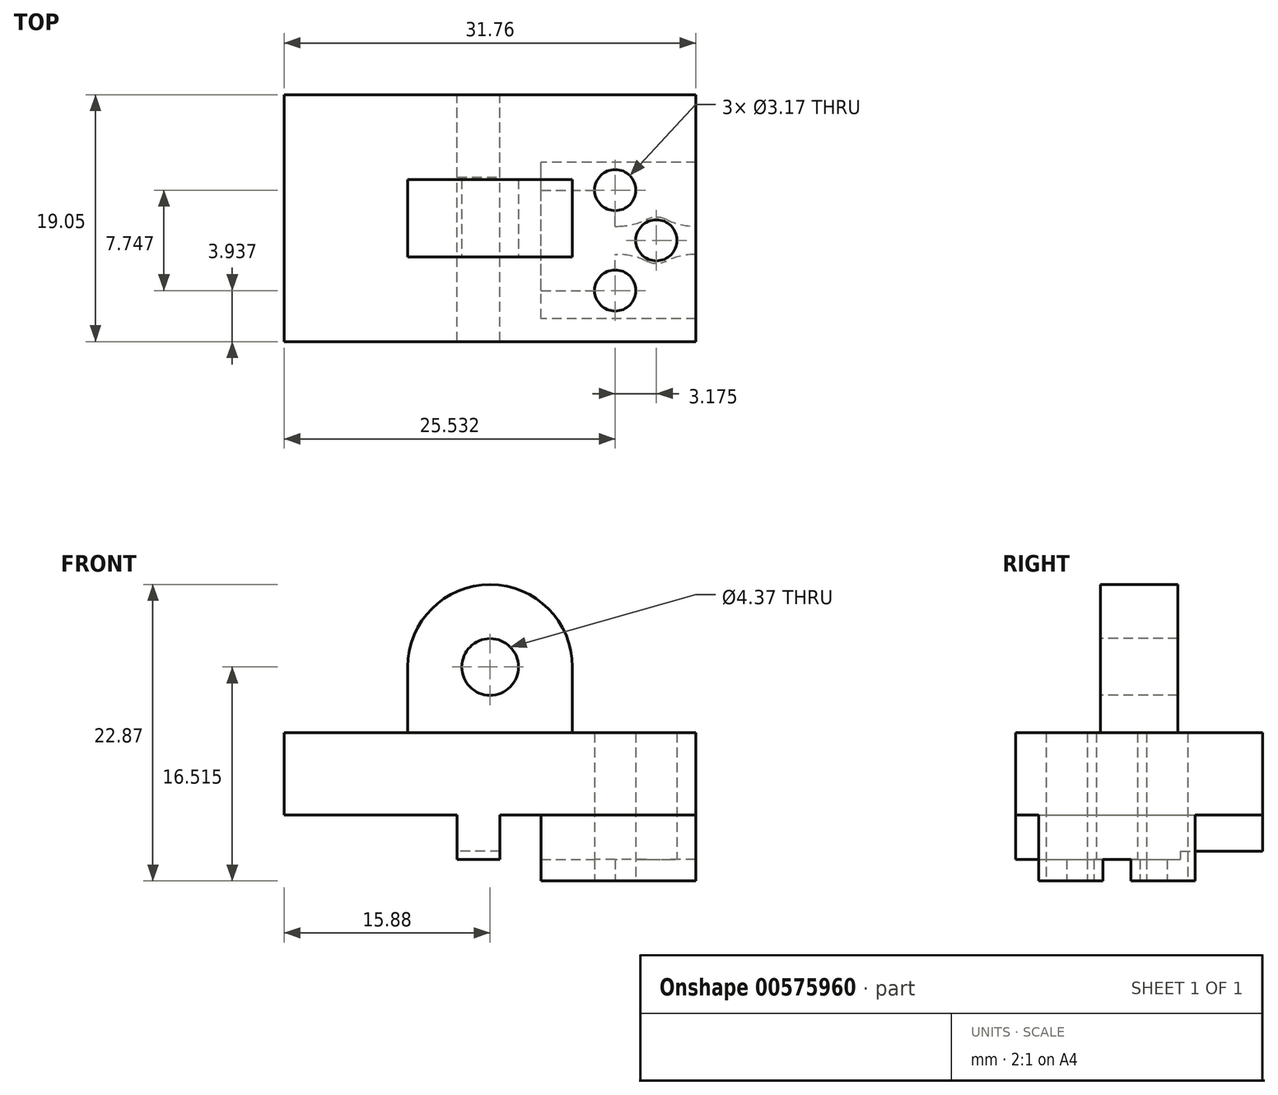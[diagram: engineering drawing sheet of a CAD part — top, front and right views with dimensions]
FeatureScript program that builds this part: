
annotation { "Feature Type Name" : "Feature", "Feature Type Description" : "" }
export const myFeature = defineFeature(function(context is Context, id is Id, definition is map)
    precondition{}
    {
        {
            var Q0;
            Q0=qCreatedBy(makeId("Front.planeOp"),FACE);
            var sketch = newSketch(context, id + "F0", { "sketchPlane" : qUnion([Q0])});
            skLineSegment(sketch, "E0.bottom", {"start": v(15.88, -3.18) * mm, "end": v(-15.88, -3.18) * mm});
            skLineSegment(sketch, "E0.top", {"start": v(15.88, 3.18) * mm, "end": v(-15.88, 3.18) * mm});
            skLineSegment(sketch, "E0.left", {"start": v(15.88, -3.18) * mm, "end": v(15.88, 3.18) * mm});
            skLineSegment(sketch, "E0.right", {"start": v(-15.88, -3.18) * mm, "end": v(-15.88, 3.17) * mm});
            skPoint(sketch, "E0.middle", {"position": v(0, 0) * mm});
            skSolve(sketch);
        }
        {
            var Q0;
            Q0=makeQuery(id+"F0.imprint","IMPRINT",FACE,{"disambiguationData":[TD([[makeQuery(id+"F0.imprint","IMPRINT",EDGE,{"derivedFrom":sQuery(id+"F0.wireOp",EDGE,"E0.bottom")}),-1.0]])]});
            extrude(context, id + "F1", {"entities" : qUnion([Q0]), "depth" : 19.05 * mm, "offsetDistance" : 25.4 * mm});
        }
        {
            var Q0;
            Q0=makeQuery(id+"F1.opExtrude","SWEPT_FACE",FACE,{"disambiguationData":[OSD([sQuery(id+"F0.wireOp",EDGE,"E0.top")])]});
            var sketch = newSketch(context, id + "F2", { "sketchPlane" : qUnion([Q0])});
            skLineSegment(sketch, "E1.bottom", {"start": v(6.35, -12.5) * mm, "end": v(-6.35, -12.5) * mm});
            skLineSegment(sketch, "E1.top", {"start": v(6.35, -6.54) * mm, "end": v(-6.35, -6.54) * mm});
            skLineSegment(sketch, "E1.left", {"start": v(6.35, -12.5) * mm, "end": v(6.35, -6.54) * mm});
            skLineSegment(sketch, "E1.right", {"start": v(-6.35, -12.5) * mm, "end": v(-6.35, -6.54) * mm});
            skPoint(sketch, "E1.middle", {"position": v(0, -9.53) * mm});
            skPoint(sketch, "E1.middle.positionSnap0", {"position": v(-15.88, -9.53) * mm});
            skPoint(sketch, "E1.centerSnap0", {"position": v(-15.88, -9.53) * mm});
            skSolve(sketch);
        }
        {
            var Q0;
            Q0=qSketchRegion(id+"F2",true);
            extrude(context, id + "F3", {"entities" : qUnion([Q0]), "operationType" : NewBodyOperationType.ADD, "depth" : 11.43 * mm, "offsetDistance" : 25.4 * mm});
        }
        {
            var Q0;
            Q0=makeQuery(id+"F3.opExtrude","CAP_EDGE",EDGE,{"disambiguationData":[OSD([sQuery(id+"F2.wireOp",EDGE,"E1.right")])],"isStart":false});
            var Q1;
            Q1=makeQuery(id+"F3.opExtrude","CAP_EDGE",EDGE,{"disambiguationData":[OSD([sQuery(id+"F2.wireOp",EDGE,"E1.left")])],"isStart":false});
            fillet(context, id + "F4", {"entities" : qUnion([Q0, Q1]), "radius" : 6.35 * mm, "tangentPropagation" : true, "allowEdgeOverflow" : false});
        }
        {
            var Q0;
            Q0=makeQuery(id+"F3.opExtrude","SWEPT_FACE",FACE,{"disambiguationData":[OSD([sQuery(id+"F2.wireOp",EDGE,"E1.bottom")])]});
            var sketch = newSketch(context, id + "F5", { "sketchPlane" : qUnion([Q0])});
            skCircle(sketch, "E2", {"center": v(0, 8.26) * mm, "radius": 2.18 * mm});
            skSolve(sketch);
        }
        {
            var Q0;
            Q0=qSketchRegion(id+"F5",true);
            extrude(context, id + "F6", {"entities" : qUnion([Q0]), "operationType" : NewBodyOperationType.REMOVE, "oppositeDirection" : true, "depth" : 25.4 * mm, "offsetDistance" : 25.4 * mm});
        }
        {
            var Q0;
            Q0=makeQuery(id+"F1.opExtrude","SWEPT_FACE",FACE,{"disambiguationData":[OSD([sQuery(id+"F0.wireOp",EDGE,"E0.bottom")])]});
            var sketch = newSketch(context, id + "F7", { "sketchPlane" : qUnion([Q0])});
            skLineSegment(sketch, "E3.bottom", {"start": v(15.88, 17.27) * mm, "end": v(3.94, 17.27) * mm});
            skLineSegment(sketch, "E3.top", {"start": v(15.88, 5.2) * mm, "end": v(3.94, 5.2) * mm});
            skLineSegment(sketch, "E3.left", {"start": v(15.88, 17.27) * mm, "end": v(15.88, 5.2) * mm});
            skLineSegment(sketch, "E3.right", {"start": v(3.94, 17.27) * mm, "end": v(3.94, 5.2) * mm});
            skSolve(sketch);
        }
        {
            var Q0;
            Q0=makeQuery(id+"F7.imprint","IMPRINT",FACE,{"disambiguationData":[TD([[makeQuery(id+"F7.imprint","IMPRINT",EDGE,{"derivedFrom":sQuery(id+"F7.wireOp",EDGE,"E3.bottom")}),1.0]])]});
            extrude(context, id + "F8", {"entities" : qUnion([Q0]), "operationType" : NewBodyOperationType.ADD, "depth" : 5.08 * mm, "offsetDistance" : 25.4 * mm});
        }
        {
            var Q0;
            Q0=makeQuery(id+"F8.opExtrude","CAP_FACE",FACE,{"disambiguationData":[OSD([sQuery(id+"F7.wireOp",EDGE,"E3.bottom"),sQuery(id+"F7.wireOp",EDGE,"E3.top"),sQuery(id+"F7.wireOp",EDGE,"E3.left"),sQuery(id+"F7.wireOp",EDGE,"E3.right")])],"isStart":false});
            var sketch = newSketch(context, id + "F9", { "sketchPlane" : qUnion([Q0])});
            skLineSegment(sketch, "E4.bottom", {"start": v(3.94, 15.11) * mm, "end": v(9.65, 15.11) * mm});
            skLineSegment(sketch, "E4.top", {"start": v(3.94, 7.37) * mm, "end": v(9.65, 7.37) * mm});
            skLineSegment(sketch, "E4.left", {"start": v(3.94, 15.11) * mm, "end": v(3.94, 7.37) * mm});
            skLineSegment(sketch, "E4.right", {"start": v(9.65, 15.11) * mm, "end": v(9.65, 7.37) * mm});
            skSolve(sketch);
        }
        {
            var Q0;
            Q0=makeQuery(id+"F9.imprint","IMPRINT",FACE,{"disambiguationData":[TD([[makeQuery(id+"F9.imprint","IMPRINT",EDGE,{"derivedFrom":sQuery(id+"F9.wireOp",EDGE,"E4.bottom")}),-1.0]])]});
            extrude(context, id + "F10", {"entities" : qUnion([Q0]), "operationType" : NewBodyOperationType.REMOVE, "oppositeDirection" : true, "depth" : 1.65 * mm, "offsetDistance" : 25.4 * mm});
        }
        {
            var Q0;
            Q0=makeQuery(id+"F8.opExtrude","CAP_FACE",FACE,{"disambiguationData":[OSD([sQuery(id+"F7.wireOp",EDGE,"E3.bottom"),sQuery(id+"F7.wireOp",EDGE,"E3.top"),sQuery(id+"F7.wireOp",EDGE,"E3.left"),sQuery(id+"F7.wireOp",EDGE,"E3.right")])],"isStart":false});
            var sketch = newSketch(context, id + "F11", { "sketchPlane" : qUnion([Q0])});
            skCircle(sketch, "E5", {"center": v(9.65, 15.11) * mm, "radius": 1.59 * mm});
            skCircle(sketch, "E6", {"center": v(9.65, 7.37) * mm, "radius": 1.59 * mm});
            skCircle(sketch, "E7", {"center": v(12.83, 11.24) * mm, "radius": 1.59 * mm});
            skPoint(sketch, "E7.centerSnap0", {"position": v(9.65, 11.24) * mm});
            skSolve(sketch);
        }
        {
            var Q0;
            Q0 = qSketchRegion(id + "F11", true);
            extrude(context, id + "F12", {"entities" : qUnion([Q0]), "operationType" : NewBodyOperationType.REMOVE, "oppositeDirection" : true, "depth" : 25.4 * mm, "offsetDistance" : 25.4 * mm});
        }
        {
            var Q0;
            Q0=makeQuery(id+"F1.opExtrude","SWEPT_FACE",FACE,{"disambiguationData":[OSD([sQuery(id+"F0.wireOp",EDGE,"E0.bottom")])]});
            var sketch = newSketch(context, id + "F13", { "sketchPlane" : qUnion([Q0])});
            skLineSegment(sketch, "E8.bottom", {"start": v(-2.54, 19.05) * mm, "end": v(0.76, 19.05) * mm});
            skLineSegment(sketch, "E8.top", {"start": v(-2.54, 0) * mm, "end": v(0.76, 0) * mm});
            skLineSegment(sketch, "E8.left", {"start": v(-2.54, 19.05) * mm, "end": v(-2.54, 0) * mm});
            skLineSegment(sketch, "E8.right", {"start": v(0.76, 19.05) * mm, "end": v(0.76, 0) * mm});
            skSolve(sketch);
        }
        {
            var Q0;
            Q0 = qSketchRegion(id + "F13", true);
            extrude(context, id + "F14", {"entities" : qUnion([Q0]), "operationType" : NewBodyOperationType.ADD, "depth" : 3.43 * mm, "offsetDistance" : 25.4 * mm});
        }
        {
            var Q0;
            Q0=makeQuery(id+"F14.opExtrude","CAP_FACE",FACE,{"disambiguationData":[OSD([sQuery(id+"F13.wireOp",EDGE,"E8.bottom"),sQuery(id+"F13.wireOp",EDGE,"E8.top"),sQuery(id+"F13.wireOp",EDGE,"E8.left"),sQuery(id+"F13.wireOp",EDGE,"E8.right")])],"isStart":false});
            var sketch = newSketch(context, id + "F15", { "sketchPlane" : qUnion([Q0])});
            skLineSegment(sketch, "E9.bottom", {"start": v(-2.54, 0) * mm, "end": v(0.76, 0) * mm});
            skLineSegment(sketch, "E9.top", {"start": v(-2.54, 6.35) * mm, "end": v(0.76, 6.35) * mm});
            skLineSegment(sketch, "E9.left", {"start": v(-2.54, 0) * mm, "end": v(-2.54, 6.35) * mm});
            skLineSegment(sketch, "E9.right", {"start": v(0.76, 0) * mm, "end": v(0.76, 6.35) * mm});
            skSolve(sketch);
        }
        {
            var Q0;
            Q0=makeQuery(id+"F15.imprint","IMPRINT",FACE,{"disambiguationData":[TD([[makeQuery(id+"F15.imprint","IMPRINT",EDGE,{"derivedFrom":sQuery(id+"F15.wireOp",EDGE,"E9.bottom")}),-1.0]])]});
            extrude(context, id + "F16", {"entities" : qUnion([Q0]), "operationType" : NewBodyOperationType.REMOVE, "oppositeDirection" : true, "depth" : 0.64 * mm, "offsetDistance" : 25.4 * mm});
        }
        {
            var Q0;
            Q0=makeQuery(id+"F8.opExtrude","CAP_FACE",FACE,{"disambiguationData":[OSD([sQuery(id+"F7.wireOp",EDGE,"E3.bottom"),sQuery(id+"F7.wireOp",EDGE,"E3.top"),sQuery(id+"F7.wireOp",EDGE,"E3.left"),sQuery(id+"F7.wireOp",EDGE,"E3.right")])],"isStart":false});
            var sketch = newSketch(context, id + "F17", { "sketchPlane" : qUnion([Q0])});
            skLineSegment(sketch, "E10.bottom", {"start": v(9.65, 12.32) * mm, "end": v(11.41, 12.32) * mm});
            skLineSegment(sketch, "E10.top", {"start": v(9.65, 10.16) * mm, "end": v(11.41, 10.16) * mm});
            skLineSegment(sketch, "E10.left", {"start": v(9.65, 12.32) * mm, "end": v(9.65, 10.16) * mm});
            skLineSegment(sketch, "E10.right", {"start": v(15.88, 12.32) * mm, "end": v(15.88, 10.16) * mm});
            skArc(sketch, "E11", {"start": v(11.41, 10.16) * mm, "mid": v(12.83, 9.46) * mm, "end": v(14.24, 10.16) * mm});
            skLineSegment(sketch, "E12.trimOffspring", {"start": v(14.24, 12.32) * mm, "end": v(15.88, 12.32) * mm});
            skLineSegment(sketch, "E13.trimOffspring", {"start": v(14.24, 10.16) * mm, "end": v(15.88, 10.16) * mm});
            skArc(sketch, "E14.trimOffspring", {"start": v(14.24, 12.32) * mm, "mid": v(12.83, 13.02) * mm, "end": v(11.41, 12.32) * mm});
            skSolve(sketch);
        }
        {
            var Q0;
            Q0 = qSketchRegion(id + "F17", true);
            extrude(context, id + "F18", {"entities" : qUnion([Q0]), "operationType" : NewBodyOperationType.REMOVE, "oppositeDirection" : true, "depth" : 1.65 * mm, "offsetDistance" : 25.4 * mm});
        }
        {
            var Q0;
            Q0=makeQuery(id+"F18.boolean.opBoolean","COPY",EDGE,{"derivedFrom":makeQuery(id+"F18.opExtrude","SWEPT_EDGE",EDGE,{"disambiguationData":[OSD([sQuery(id+"F17.wireOp",EDGE,"E10.bottom"),sQuery(id+"F17.wireOp",EDGE,"E14.trimOffspring")])]})});
            var Q1;
            Q1=makeQuery(id+"F18.boolean.opBoolean","COPY",EDGE,{"derivedFrom":makeQuery(id+"F18.opExtrude","SWEPT_EDGE",EDGE,{"disambiguationData":[OSD([sQuery(id+"F17.wireOp",EDGE,"E12.trimOffspring"),sQuery(id+"F17.wireOp",EDGE,"E14.trimOffspring")])]})});
            var Q2;
            Q2=makeQuery(id+"F18.boolean.opBoolean","COPY",EDGE,{"derivedFrom":makeQuery(id+"F18.opExtrude","SWEPT_EDGE",EDGE,{"disambiguationData":[OSD([sQuery(id+"F17.wireOp",EDGE,"E10.top"),sQuery(id+"F17.wireOp",EDGE,"E11")])]})});
            var Q3;
            Q3=makeQuery(id+"F18.boolean.opBoolean","COPY",EDGE,{"derivedFrom":makeQuery(id+"F18.opExtrude","SWEPT_EDGE",EDGE,{"disambiguationData":[OSD([sQuery(id+"F17.wireOp",EDGE,"E11"),sQuery(id+"F17.wireOp",EDGE,"E13.trimOffspring")])]})});
            fillet(context, id + "F19", {"entities" : qUnion([Q0, Q1, Q2, Q3]), "radius" : 5.08 * mm, "tangentPropagation" : true, "allowEdgeOverflow" : false});
        }
    });
